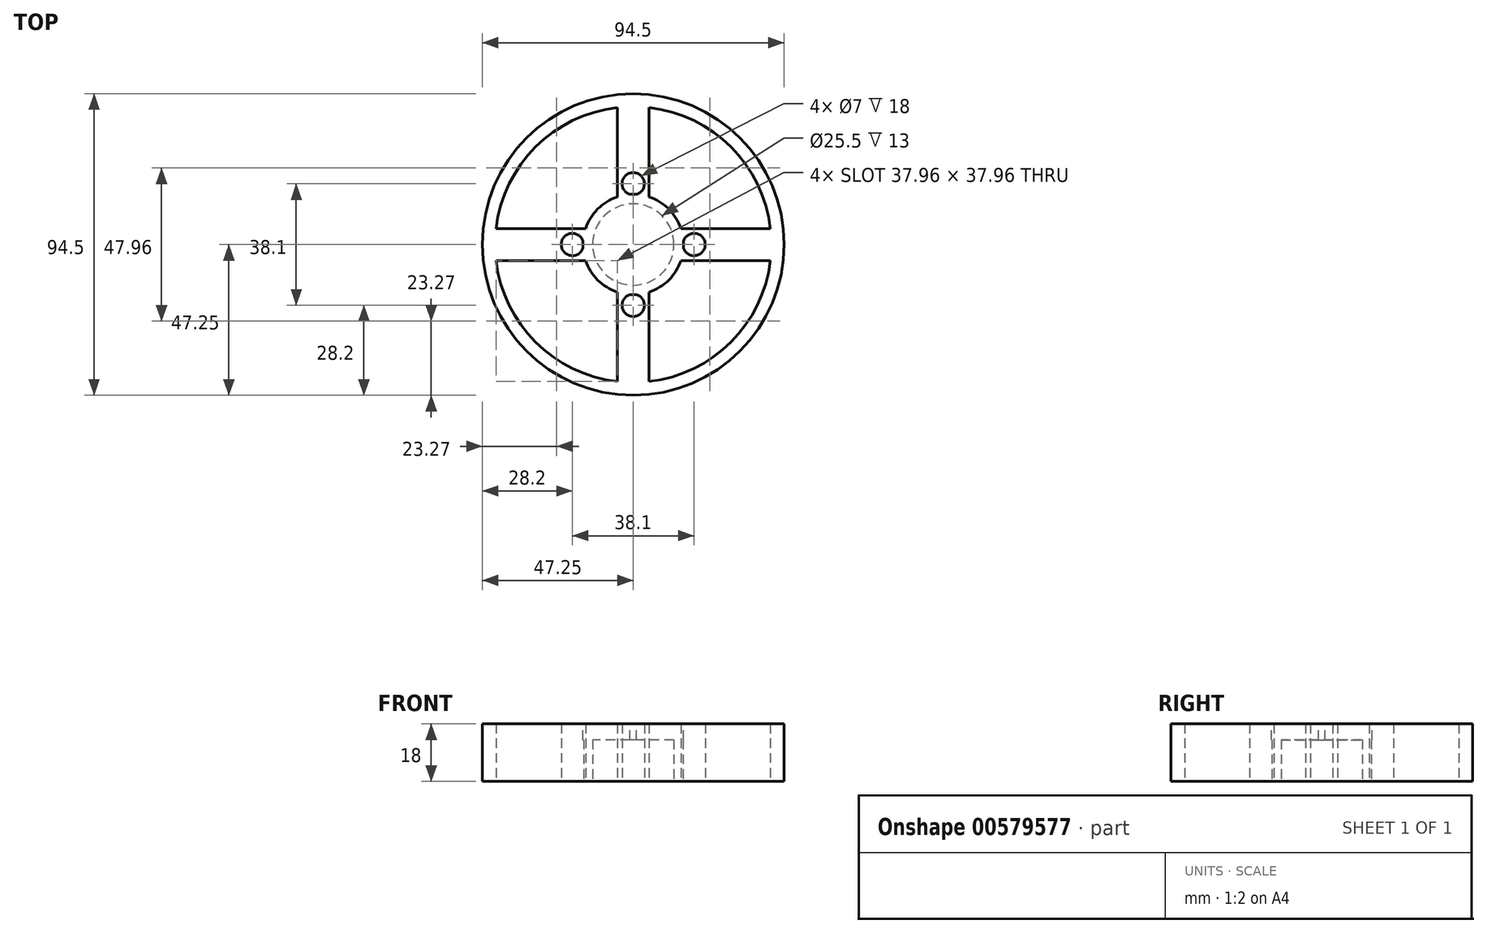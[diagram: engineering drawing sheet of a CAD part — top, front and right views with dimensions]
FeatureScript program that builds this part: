
annotation { "Feature Type Name" : "Feature", "Feature Type Description" : "" }
export const myFeature = defineFeature(function(context is Context, id is Id, definition is map)
    precondition{}
    {
        {
            var Q0;
            Q0=qCreatedBy(makeId("Top.planeOp"),FACE);
            var sketch = newSketch(context, id + "F0", { "sketchPlane" : qUnion([Q0])});
            skCircle(sketch, "E0", {"center": v(0, 0) * mm, "radius": 47.25 * mm});
            skCircle(sketch, "E1", {"center": v(0, 0) * mm, "radius": 12.75 * mm});
            skCircle(sketch, "E2", {"center": v(0, 0) * mm, "radius": 43.25 * mm});
            skLineSegment(sketch, "E3", {"start": v(-5, 0) * mm, "end": v(-5, 42.96) * mm});
            skLineSegment(sketch, "E4", {"start": v(5, 0) * mm, "end": v(5, 42.96) * mm});
            skLineSegment(sketch, "E5", {"start": v(-5, 0) * mm, "end": v(-5, -42.96) * mm});
            skLineSegment(sketch, "E6", {"start": v(5, 0) * mm, "end": v(5, -42.96) * mm});
            skLineSegment(sketch, "E7", {"start": v(0, 5) * mm, "end": v(42.96, 5) * mm});
            skLineSegment(sketch, "E8", {"start": v(0, -5) * mm, "end": v(42.96, -5) * mm});
            skLineSegment(sketch, "E9", {"start": v(0, 5) * mm, "end": v(-42.96, 5) * mm});
            skLineSegment(sketch, "E10", {"start": v(0, -5) * mm, "end": v(-42.96, -5) * mm});
            skCircle(sketch, "E11", {"center": v(0, 0) * mm, "radius": 15.75 * mm});
            skPoint(sketch, "E12", {"position": v(0, 19.05) * mm});
            skPoint(sketch, "E13", {"position": v(19.05, 0) * mm});
            skPoint(sketch, "E14", {"position": v(0, -19.05) * mm});
            skPoint(sketch, "E15", {"position": v(-19.05, 0) * mm});
            skCircle(sketch, "E16", {"center": v(0, 19.05) * mm, "radius": 3.5 * mm});
            skCircle(sketch, "E17", {"center": v(19.05, 0) * mm, "radius": 3.5 * mm});
            skCircle(sketch, "E18", {"center": v(0, -19.05) * mm, "radius": 3.5 * mm});
            skCircle(sketch, "E19", {"center": v(-19.05, 0) * mm, "radius": 3.5 * mm});
            skSolve(sketch);
        }
        {
            var Q0;
            {var subQ0=sQuery(id+"F0.wireOp",EDGE,"E4");var subQ1=sQuery(id+"F0.wireOp",EDGE,"E1");var subQ2=makeQuery(id+"F0.imprint","INTERSECT",VERTEX,{"derivedFrom":[subQ1,subQ0]});Q0=makeQuery(id+"F0.imprint","IMPRINT",FACE,{"disambiguationData":[TD([[makeQuery(id+"F0.imprint","IMPRINT",EDGE,{"disambiguationData":[TD([[subQ2,-1.0]])],"derivedFrom":subQ1}),-1.0]])]});}
            var Q1;
            {var subQ0=sQuery(id+"F0.wireOp",EDGE,"E7");var subQ1=sQuery(id+"F0.wireOp",EDGE,"E1");var subQ2=makeQuery(id+"F0.imprint","INTERSECT",VERTEX,{"derivedFrom":[subQ1,subQ0]});Q1=makeQuery(id+"F0.imprint","IMPRINT",FACE,{"disambiguationData":[TD([[makeQuery(id+"F0.imprint","IMPRINT",EDGE,{"disambiguationData":[TD([[subQ2,1.0]])],"derivedFrom":subQ1}),-1.0]])]});}
            var Q2;
            {var subQ0=sQuery(id+"F0.wireOp",EDGE,"E9");var subQ1=sQuery(id+"F0.wireOp",EDGE,"E1");var subQ2=makeQuery(id+"F0.imprint","INTERSECT",VERTEX,{"derivedFrom":[subQ1,subQ0]});Q2=makeQuery(id+"F0.imprint","IMPRINT",FACE,{"disambiguationData":[TD([[makeQuery(id+"F0.imprint","IMPRINT",EDGE,{"disambiguationData":[TD([[subQ2,-1.0]])],"derivedFrom":subQ1}),-1.0]])]});}
            var Q3;
            {var subQ0=sQuery(id+"F0.wireOp",EDGE,"E5");var subQ1=sQuery(id+"F0.wireOp",EDGE,"E1");var subQ2=makeQuery(id+"F0.imprint","INTERSECT",VERTEX,{"derivedFrom":[subQ1,subQ0]});Q3=makeQuery(id+"F0.imprint","IMPRINT",FACE,{"disambiguationData":[TD([[makeQuery(id+"F0.imprint","IMPRINT",EDGE,{"disambiguationData":[TD([[subQ2,-1.0]])],"derivedFrom":subQ1}),-1.0]])]});}
            var Q4;
            {var subQ0=sQuery(id+"F0.wireOp",EDGE,"E10");var subQ1=sQuery(id+"F0.wireOp",EDGE,"E1");var subQ2=makeQuery(id+"F0.imprint","INTERSECT",VERTEX,{"derivedFrom":[subQ1,subQ0]});Q4=makeQuery(id+"F0.imprint","IMPRINT",FACE,{"disambiguationData":[TD([[makeQuery(id+"F0.imprint","IMPRINT",EDGE,{"disambiguationData":[TD([[subQ2,-1.0]])],"derivedFrom":subQ1}),-1.0]])]});}
            var Q5;
            {var subQ0=sQuery(id+"F0.wireOp",EDGE,"E6");var subQ1=sQuery(id+"F0.wireOp",EDGE,"E1");var subQ2=makeQuery(id+"F0.imprint","INTERSECT",VERTEX,{"derivedFrom":[subQ1,subQ0]});Q5=makeQuery(id+"F0.imprint","IMPRINT",FACE,{"disambiguationData":[TD([[makeQuery(id+"F0.imprint","IMPRINT",EDGE,{"disambiguationData":[TD([[subQ2,-1.0]])],"derivedFrom":subQ1}),-1.0]])]});}
            var Q6;
            {var subQ0=sQuery(id+"F0.wireOp",EDGE,"E4");var subQ1=sQuery(id+"F0.wireOp",EDGE,"E1");var subQ2=makeQuery(id+"F0.imprint","INTERSECT",VERTEX,{"derivedFrom":[subQ1,subQ0]});Q6=makeQuery(id+"F0.imprint","IMPRINT",FACE,{"disambiguationData":[TD([[makeQuery(id+"F0.imprint","IMPRINT",EDGE,{"disambiguationData":[TD([[subQ2,1.0]])],"derivedFrom":subQ1}),-1.0]])]});}
            var Q7;
            {var subQ0=sQuery(id+"F0.wireOp",EDGE,"E3");var subQ1=sQuery(id+"F0.wireOp",EDGE,"E1");var subQ2=makeQuery(id+"F0.imprint","INTERSECT",VERTEX,{"derivedFrom":[subQ1,subQ0]});Q7=makeQuery(id+"F0.imprint","IMPRINT",FACE,{"disambiguationData":[TD([[makeQuery(id+"F0.imprint","IMPRINT",EDGE,{"disambiguationData":[TD([[subQ2,-1.0]])],"derivedFrom":subQ1}),-1.0]])]});}
            var Q8;
            {var subQ0=sQuery(id+"F0.wireOp",EDGE,"E7");var subQ1=sQuery(id+"F0.wireOp",EDGE,"E2");var subQ2=makeQuery(id+"F0.imprint","INTERSECT",VERTEX,{"derivedFrom":[subQ1,subQ0]});Q8=makeQuery(id+"F0.imprint","IMPRINT",FACE,{"disambiguationData":[TD([[makeQuery(id+"F0.imprint","IMPRINT",EDGE,{"disambiguationData":[TD([[subQ2,1.0]])],"derivedFrom":subQ1}),1.0]])]});}
            var Q9;
            {var subQ0=sQuery(id+"F0.wireOp",EDGE,"E9");var subQ1=sQuery(id+"F0.wireOp",EDGE,"E2");var subQ2=makeQuery(id+"F0.imprint","INTERSECT",VERTEX,{"derivedFrom":[subQ1,subQ0]});Q9=makeQuery(id+"F0.imprint","IMPRINT",FACE,{"disambiguationData":[TD([[makeQuery(id+"F0.imprint","IMPRINT",EDGE,{"disambiguationData":[TD([[subQ2,-1.0]])],"derivedFrom":subQ1}),1.0]])]});}
            var Q10;
            {var subQ0=sQuery(id+"F0.wireOp",EDGE,"E3");var subQ1=sQuery(id+"F0.wireOp",EDGE,"E2");var subQ2=makeQuery(id+"F0.imprint","INTERSECT",VERTEX,{"derivedFrom":[subQ1,subQ0]});Q10=makeQuery(id+"F0.imprint","IMPRINT",FACE,{"disambiguationData":[TD([[makeQuery(id+"F0.imprint","IMPRINT",EDGE,{"disambiguationData":[TD([[subQ2,1.0]])],"derivedFrom":subQ1}),1.0]])]});}
            var Q11;
            {var subQ0=sQuery(id+"F0.wireOp",EDGE,"E5");var subQ1=sQuery(id+"F0.wireOp",EDGE,"E2");var subQ2=makeQuery(id+"F0.imprint","INTERSECT",VERTEX,{"derivedFrom":[subQ1,subQ0]});Q11=makeQuery(id+"F0.imprint","IMPRINT",FACE,{"disambiguationData":[TD([[makeQuery(id+"F0.imprint","IMPRINT",EDGE,{"disambiguationData":[TD([[subQ2,-1.0]])],"derivedFrom":subQ1}),1.0]])]});}
            var Q12;
            Q12=makeQuery(id+"F0.imprint","IMPRINT",FACE,{"disambiguationData":[TD([[makeQuery(id+"F0.imprint","IMPRINT",EDGE,{"derivedFrom":sQuery(id+"F0.wireOp",EDGE,"E0")}),1.0]])]});
            extrude(context, id + "F1", {"entities" : qUnion([Q0, Q1, Q2, Q3, Q4, Q5, Q6, Q7, Q8, Q9, Q10, Q11, Q12]), "depth" : 18 * mm, "offsetDistance" : 25 * mm});
        }
        {
            var Q0;
            Q0=makeQuery(id+"F1.opExtrude","CAP_FACE",FACE,{"disambiguationData":[OSD([sQuery(id+"F0.wireOp",EDGE,"E0"),sQuery(id+"F0.wireOp",EDGE,"E1"),sQuery(id+"F0.wireOp",EDGE,"E2"),sQuery(id+"F0.wireOp",EDGE,"E3"),sQuery(id+"F0.wireOp",EDGE,"E4"),sQuery(id+"F0.wireOp",EDGE,"E5"),sQuery(id+"F0.wireOp",EDGE,"E6"),sQuery(id+"F0.wireOp",EDGE,"E7"),sQuery(id+"F0.wireOp",EDGE,"E8"),sQuery(id+"F0.wireOp",EDGE,"E9"),sQuery(id+"F0.wireOp",EDGE,"E10"),sQuery(id+"F0.wireOp",EDGE,"E11"),sQuery(id+"F0.wireOp",EDGE,"E16"),sQuery(id+"F0.wireOp",EDGE,"E17"),sQuery(id+"F0.wireOp",EDGE,"E18"),sQuery(id+"F0.wireOp",EDGE,"E19")])],"isStart":false});
            var sketch = newSketch(context, id + "F2", { "sketchPlane" : qUnion([Q0])});
            skCircle(sketch, "E20", {"center": v(0, 0) * mm, "radius": 15.75 * mm});
            skSolve(sketch);
        }
        {
            var Q0;
            Q0 = qSketchRegion(id + "F2", true);
            extrude(context, id + "F3", {"entities" : qUnion([Q0]), "operationType" : NewBodyOperationType.ADD, "oppositeDirection" : true, "depth" : 5 * mm, "offsetDistance" : 25 * mm});
        }
    });
